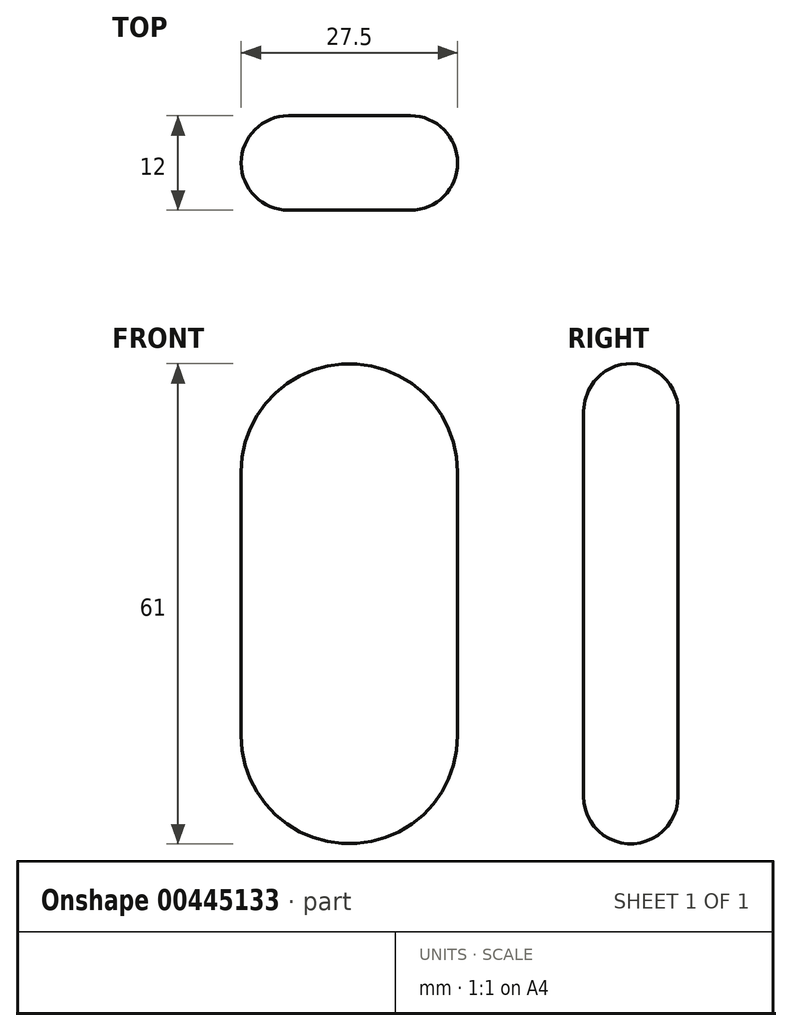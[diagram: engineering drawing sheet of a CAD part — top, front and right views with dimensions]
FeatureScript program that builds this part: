
annotation { "Feature Type Name" : "Feature", "Feature Type Description" : "" }
export const myFeature = defineFeature(function(context is Context, id is Id, definition is map)
    precondition{}
    {
        {
            var Q0;
            Q0=qCreatedBy(makeId("Front.planeOp"),FACE);
            var sketch = newSketch(context, id + "F0", { "sketchPlane" : qUnion([Q0])});
            skArc(sketch, "E0", {"start": v(-13.75, 0) * mm, "mid": v(0, -13.75) * mm, "end": v(13.75, 0) * mm});
            skArc(sketch, "E1", {"start": v(13.75, 33.5) * mm, "mid": v(0, 47.25) * mm, "end": v(-13.75, 33.5) * mm});
            skLineSegment(sketch, "E2", {"start": v(-13.75, 33.5) * mm, "end": v(-13.75, 0) * mm});
            skLineSegment(sketch, "E3", {"start": v(13.75, 33.5) * mm, "end": v(13.75, 0) * mm});
            skSolve(sketch);
        }
        {
            var Q0;
            Q0=qSketchRegion(id+"F0",true);
            extrude(context, id + "F1", {"entities" : qUnion([Q0]), "depth" : 12 * mm});
        }
        {
            var Q0;
            Q0=makeQuery(id+"F1.opExtrude","CAP_EDGE",EDGE,{"disambiguationData":[OSD([sQuery(id+"F0.wireOp",EDGE,"E3")])],"isStart":false});
            var Q1;
            Q1=makeQuery(id+"F1.opExtrude","CAP_EDGE",EDGE,{"disambiguationData":[OSD([sQuery(id+"F0.wireOp",EDGE,"E3")])],"isStart":true});
            fillet(context, id + "F2", {"entities" : qUnion([Q0, Q1]), "radius" : 6 * mm, "tangentPropagation" : true, "allowEdgeOverflow" : false});
        }
    });
